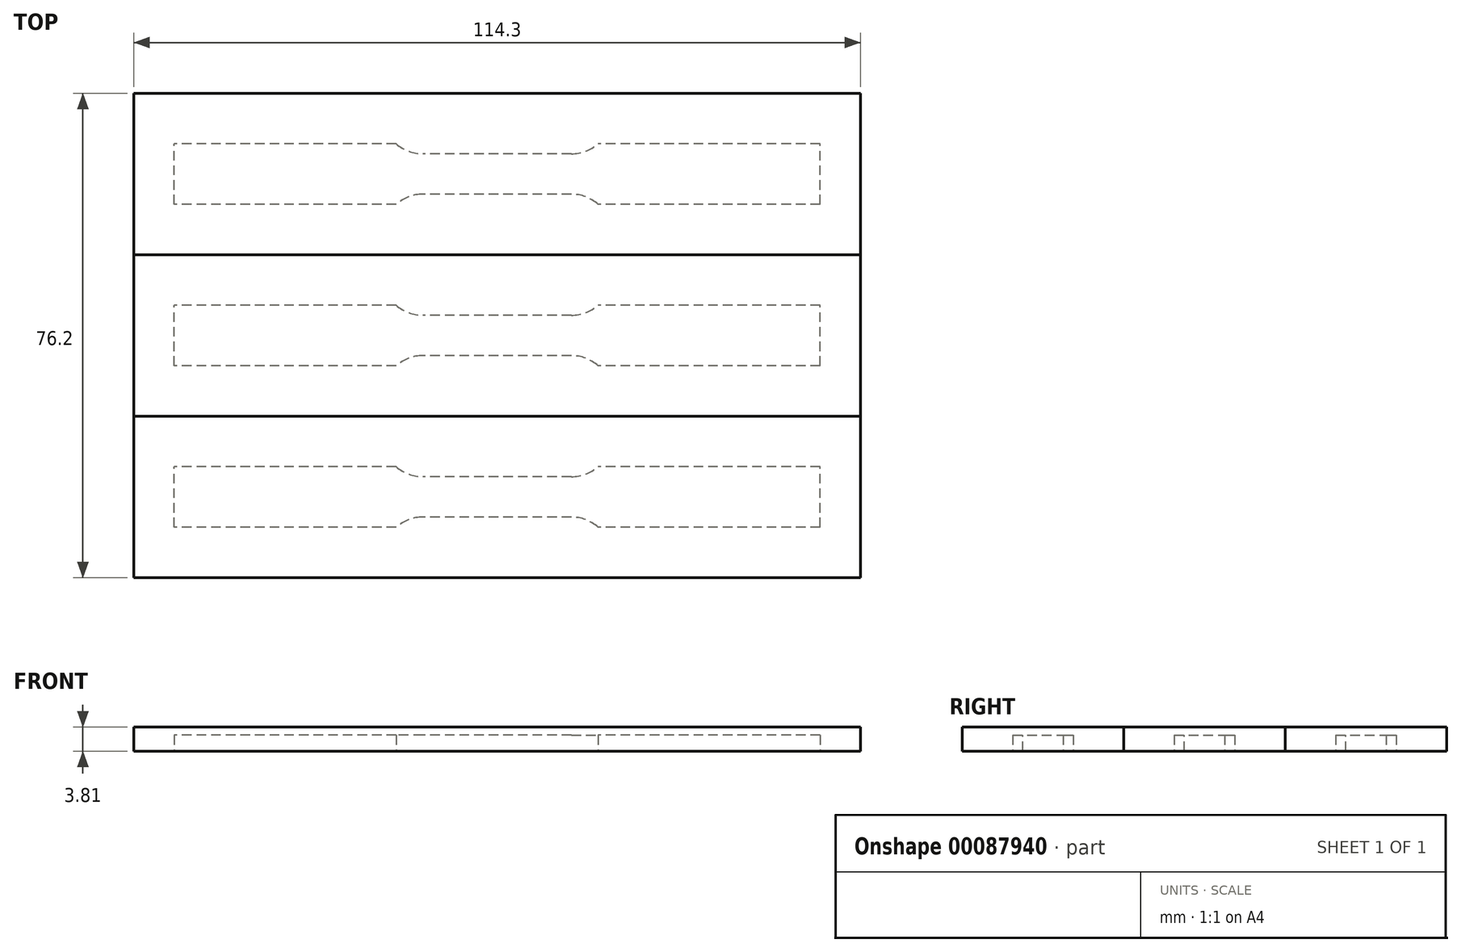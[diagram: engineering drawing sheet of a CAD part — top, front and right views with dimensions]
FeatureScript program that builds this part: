
annotation { "Feature Type Name" : "Feature", "Feature Type Description" : "" }
export const myFeature = defineFeature(function(context is Context, id is Id, definition is map)
    precondition{}
    {
        {
            var Q0;
            Q0=qCreatedBy(makeId("Top.planeOp"),FACE);
            var sketch = newSketch(context, id + "F0", { "sketchPlane" : qUnion([Q0])});
            skLineSegment(sketch, "E0.rect.bottom", {"start": v(50.8, -4.76) * mm, "end": v(-50.8, -4.76) * mm});
            skLineSegment(sketch, "E0.rect.top", {"start": v(50.8, 4.76) * mm, "end": v(-50.8, 4.76) * mm});
            skLineSegment(sketch, "E0.rect.left", {"start": v(50.8, -4.76) * mm, "end": v(50.8, 4.76) * mm});
            skLineSegment(sketch, "E0.rect.right", {"start": v(-50.8, -4.76) * mm, "end": v(-50.8, 4.76) * mm});
            skPoint(sketch, "E0.rect.middle", {"position": v(0, 0) * mm});
            skSolve(sketch);
        }
        {
            var Q0;
            Q0=qCreatedBy(makeId("Top.planeOp"),FACE);
            var sketch = newSketch(context, id + "F1", { "sketchPlane" : qUnion([Q0])});
            skLineSegment(sketch, "E1.bottom", {"start": v(57.15, -12.7) * mm, "end": v(-57.15, -12.7) * mm});
            skLineSegment(sketch, "E1.top", {"start": v(57.15, 12.7) * mm, "end": v(-57.15, 12.7) * mm});
            skLineSegment(sketch, "E1.left", {"start": v(57.15, -12.7) * mm, "end": v(57.15, 12.7) * mm});
            skLineSegment(sketch, "E1.right", {"start": v(-57.15, -12.7) * mm, "end": v(-57.15, 12.7) * mm});
            skPoint(sketch, "E1.middle", {"position": v(0, 0) * mm});
            skSolve(sketch);
        }
        {
            var Q0;
            Q0=makeQuery(id+"F0.imprint","IMPRINT",FACE,{"disambiguationData":[TD([[makeQuery(id+"F0.imprint","IMPRINT",EDGE,{"derivedFrom":sQuery(id+"F0.wireOp",EDGE,"E0.rect.bottom")}),-1.0]])]});
            var sketch = newSketch(context, id + "F2", { "sketchPlane" : qUnion([Q0])});
            skLineSegment(sketch, "E2.bottom", {"start": v(15.88, 3.18) * mm, "end": v(-15.88, 3.18) * mm});
            skLineSegment(sketch, "E2.top", {"start": v(15.88, 4.76) * mm, "end": v(-15.88, 4.76) * mm});
            skLineSegment(sketch, "E2.left", {"start": v(15.88, 3.17) * mm, "end": v(15.88, 4.76) * mm});
            skLineSegment(sketch, "E2.right", {"start": v(-15.88, 3.18) * mm, "end": v(-15.88, 4.76) * mm});
            skPoint(sketch, "E2.middle", {"position": v(0, 3.97) * mm});
            skLineSegment(sketch, "E3.bottom", {"start": v(15.88, -4.76) * mm, "end": v(-15.88, -4.76) * mm});
            skLineSegment(sketch, "E3.top", {"start": v(15.88, -3.17) * mm, "end": v(-15.88, -3.17) * mm});
            skLineSegment(sketch, "E3.left", {"start": v(15.88, -4.76) * mm, "end": v(15.88, -3.18) * mm});
            skLineSegment(sketch, "E3.right", {"start": v(-15.88, -4.76) * mm, "end": v(-15.88, -3.17) * mm});
            skPoint(sketch, "E3.middle", {"position": v(0, -3.97) * mm});
            skSolve(sketch);
        }
        {
            var Q0;
            Q0=makeQuery(id+"F1.imprint","IMPRINT",FACE,{"disambiguationData":[TD([[makeQuery(id+"F1.imprint","IMPRINT",EDGE,{"derivedFrom":sQuery(id+"F1.wireOp",EDGE,"E1.bottom")}),-1.0]])]});
            extrude(context, id + "F3", {"entities" : qUnion([Q0]), "depth" : 3.8 * mm});
        }
        {
            var Q0;
            Q0=makeQuery(id+"F2.imprint","IMPRINT",FACE,{"disambiguationData":[TD([[makeQuery(id+"F2.imprint","IMPRINT",EDGE,{"derivedFrom":sQuery(id+"F2.wireOp",EDGE,"E2.bottom")}),1.0]])]});
            extrude(context, id + "F4", {"entities" : qUnion([Q0]), "operationType" : NewBodyOperationType.REMOVE, "depth" : 2.54 * mm});
        }
        {
            var Q0;
            Q0=makeQuery(id+"F4.boolean.opBoolean","COPY",EDGE,{"derivedFrom":makeQuery(id+"F4.opExtrude","SWEPT_EDGE",EDGE,{"disambiguationData":[OSD([sQuery(id+"F2.wireOp",EDGE,"E3.top"),sQuery(id+"F2.wireOp",EDGE,"E3.left")])]})});
            var Q1;
            Q1=makeQuery(id+"F4.boolean.opBoolean","COPY",EDGE,{"derivedFrom":makeQuery(id+"F4.opExtrude","SWEPT_EDGE",EDGE,{"disambiguationData":[OSD([sQuery(id+"F2.wireOp",EDGE,"E2.bottom"),sQuery(id+"F2.wireOp",EDGE,"E2.left")])]})});
            var Q2;
            Q2=makeQuery(id+"F4.boolean.opBoolean","COPY",EDGE,{"derivedFrom":makeQuery(id+"F4.opExtrude","SWEPT_EDGE",EDGE,{"disambiguationData":[OSD([sQuery(id+"F2.wireOp",EDGE,"E3.top"),sQuery(id+"F2.wireOp",EDGE,"E3.right")])]})});
            var Q3;
            Q3=makeQuery(id+"F4.boolean.opBoolean","COPY",EDGE,{"derivedFrom":makeQuery(id+"F4.opExtrude","SWEPT_EDGE",EDGE,{"disambiguationData":[OSD([sQuery(id+"F2.wireOp",EDGE,"E2.bottom"),sQuery(id+"F2.wireOp",EDGE,"E2.right")])]})});
            fillet(context, id + "F5", {"entities" : qUnion([Q0, Q1, Q2, Q3]), "radius" : 6.35 * mm, "tangentPropagation" : true, "allowEdgeOverflow" : false});
        }
        {
            var Q0;
            Q0=makeQuery(id+"F3.opExtrude","SWEPT_BODY",BODY,{"disambiguationData":[OSD([sQuery(id+"F1.wireOp",EDGE,"E1.bottom"),sQuery(id+"F1.wireOp",EDGE,"E1.top"),sQuery(id+"F1.wireOp",EDGE,"E1.left"),sQuery(id+"F1.wireOp",EDGE,"E1.right")])]});
            transform(context, id + "F6", {"entities" : qUnion([Q0]), "transformType" : TransformType.TRANSLATION_3D, "dx" : 0 * mm, "dy" : 25.4 * mm, "dz" : 0 * mm, "makeCopy" : true});
        }
        {
            var Q0;
            Q0=makeQuery(id+"F3.opExtrude","SWEPT_BODY",BODY,{"disambiguationData":[OSD([sQuery(id+"F1.wireOp",EDGE,"E1.bottom"),sQuery(id+"F1.wireOp",EDGE,"E1.top"),sQuery(id+"F1.wireOp",EDGE,"E1.left"),sQuery(id+"F1.wireOp",EDGE,"E1.right")])]});
            transform(context, id + "F7", {"entities" : qUnion([Q0]), "transformType" : TransformType.TRANSLATION_3D, "dx" : 0 * mm, "dy" : -25.4 * mm, "dz" : 0 * mm, "makeCopy" : true});
        }
    });
